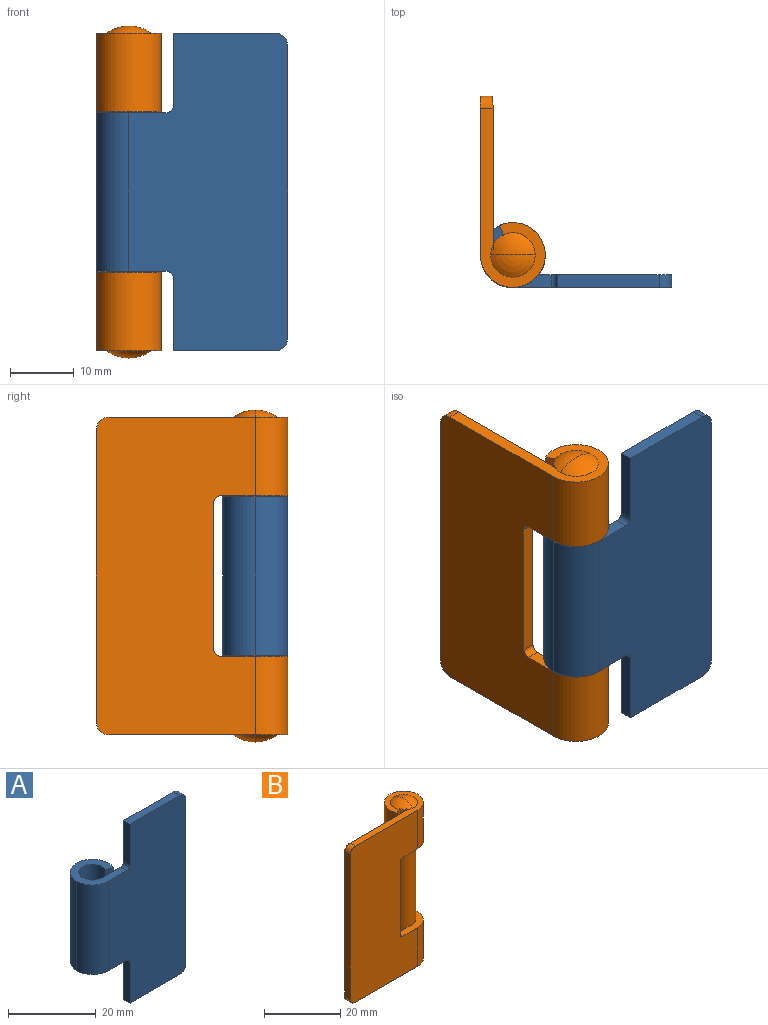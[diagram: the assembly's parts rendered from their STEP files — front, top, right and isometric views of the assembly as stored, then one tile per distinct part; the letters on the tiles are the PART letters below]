
ASSEMBLY  parts=2 mates=1
PART A: 18 faces, bbox 30.1x10.2x50 mm
  f0: plane 11.5x2mm, normal (-1,0,0), area 23mm2, adj f1,f2,f8,f9
  f1: cylinder r=1mm len=2mm, axis (0,1,0), area 3.1mm2, adj f0,f2,f7,f8
  f2: plane 50x25mm, normal (0,-1,0), area 1073.7mm2, adj f0,f1,f3,f7,f9,f10,f11,f12
  f3: cylinder r=5.1mm len=25mm, axis (0,0,1), area 200.3mm2, adj f2,f4,f7,f16
  f4: cylinder r=5.1mm len=25mm, axis (0,0,1), area 456.2mm2, adj f3,f5,f7,f16
  f5: plane 25x1.81mm, normal (-0.42,-0.91,0), area 50mm2, adj f4,f6,f7,f16
  f6: cylinder r=3.1mm len=25mm, axis (0,0,1), area 277.3mm2, adj f5,f7,f16,f17
  f7: plane 11.1x10.2mm, normal (0,0,-1), area 54.2mm2, adj f1,f2,f3,f4,f5,f6,f8,f17
  f8: plane 50x25mm, normal (0,1,0), area 1073.7mm2, adj f0,f1,f7,f9,f10,f11,f12,f13
  f9: plane 16x2mm, normal (0,0,-1), area 32mm2, adj f0,f2,f8,f10
  f10: cylinder r=2mm len=2mm, axis (0,1,0), area 6.3mm2, adj f2,f8,f9,f11
  f11: plane 46x2mm, normal (1,0,0), area 92mm2, adj f2,f8,f10,f12
  f12: cylinder r=2mm len=2mm, axis (0,1,0), area 6.3mm2, adj f2,f8,f11,f13
  f13: plane 16x2mm, normal (0,0,1), area 32mm2, adj f2,f8,f12,f14
  f14: plane 11.5x2mm, normal (-1,0,0), area 23mm2, adj f2,f8,f13,f15
  f15: cylinder r=1mm len=2mm, axis (0,1,0), area 3.1mm2, adj f2,f8,f14,f16
  f16: plane 11.1x10.2mm, normal (0,0,1), area 54.2mm2, adj f2,f3,f4,f5,f6,f8,f15,f17
  f17: cylinder r=3.1mm len=25mm, axis (0,0,1), area 121.7mm2, adj f6,f7,f8,f16
PART B: 26 faces, bbox 30.1x10.2x52.3 mm
  f0: sphere r=6mm, area 21.2mm2, adj f1,f2
  f1: sphere r=6mm, area 21.2mm2, adj f0,f2,f25
  f2: plane 28.1x10.2mm, normal (0,0,1), area 81mm2, adj f0,f1,f3,f4,f5,f6,f7,f8
  f3: plane 12.4x1.81mm, normal (0.42,-0.91,0), area 24.8mm2, adj f2,f4,f9,f11,f25
  f4: cylinder r=5.1mm len=12.4mm, axis (0,0,1), area 27.6mm2, adj f2,f3,f5,f11
  f5: cylinder r=5.1mm len=12.4mm, axis (0,0,1), area 298mm2, adj f2,f4,f6,f11
  f6: plane 50x25mm, normal (0,-1,0), area 1084.9mm2, adj f2,f5,f7,f11,f12,f13,f14,f15
  f7: cylinder r=2mm len=2mm, axis (0,1,0), area 6.3mm2, adj f2,f6,f8,f22
  f8: plane 50x25mm, normal (0,1,0), area 1084.9mm2, adj f2,f7,f9,f11,f12,f13,f14,f15
  f9: cylinder r=3.1mm len=50mm, axis (0,0,1), area 332.7mm2, adj f3,f8,f10,f11,f15,f16,f17,f25
  f10: cylinder r=3.1mm len=25.2mm, axis (0,0,1), area 245.4mm2, adj f9,f11,f15
  f11: plane 10.6x10.2mm, normal (0,0,-1), area 53.2mm2, adj f3,f4,f5,f6,f8,f9,f10,f12
  f12: cylinder r=1mm len=2mm, axis (0,1,0), area 3.1mm2, adj f6,f8,f11,f13
  f13: plane 23.2x2mm, normal (1,0,0), area 46.4mm2, adj f6,f8,f12,f14
  f14: cylinder r=1mm len=2mm, axis (0,1,0), area 3.1mm2, adj f6,f8,f13,f15
  f15: plane 10.6x10.2mm, normal (0,0,1), area 53.2mm2, adj f6,f8,f9,f10,f14,f16,f23,f24
  f16: plane 12.4x1.81mm, normal (0.42,-0.91,0), area 24.8mm2, adj f9,f15,f17,f20,f24
  f17: plane 3.17x1.79mm, normal (0,0,1), area 1.1mm2, adj f8,f9,f16,f18
  f18: sphere r=6mm, area 21.2mm2, adj f17,f19,f20
  f19: sphere r=6mm, area 21.2mm2, adj f18,f20
  f20: plane 28.1x10.2mm, normal (0,0,-1), area 81mm2, adj f6,f8,f16,f18,f19,f21,f23,f24
  f21: cylinder r=2mm len=2mm, axis (0,1,0), area 6.3mm2, adj f6,f8,f20,f22
  f22: plane 46x2mm, normal (-1,0,0), area 92mm2, adj f6,f7,f8,f21
  f23: cylinder r=5.1mm len=12.4mm, axis (0,0,1), area 298mm2, adj f6,f15,f20,f24
  f24: cylinder r=5.1mm len=12.4mm, axis (0,0,1), area 27.6mm2, adj f15,f16,f20,f23
  f25: plane 3.17x1.79mm, normal (0,0,-1), area 1.1mm2, adj f1,f3,f8,f9
PLACE A at identity fixed
PLACE B rot(axis=(0,0,-1),89.9deg) t=(-5.1,5.09,0)mm
MATE revolute B.f9 <-> A.f3  axis (0,0,1) through (0,5.1,0)mm
